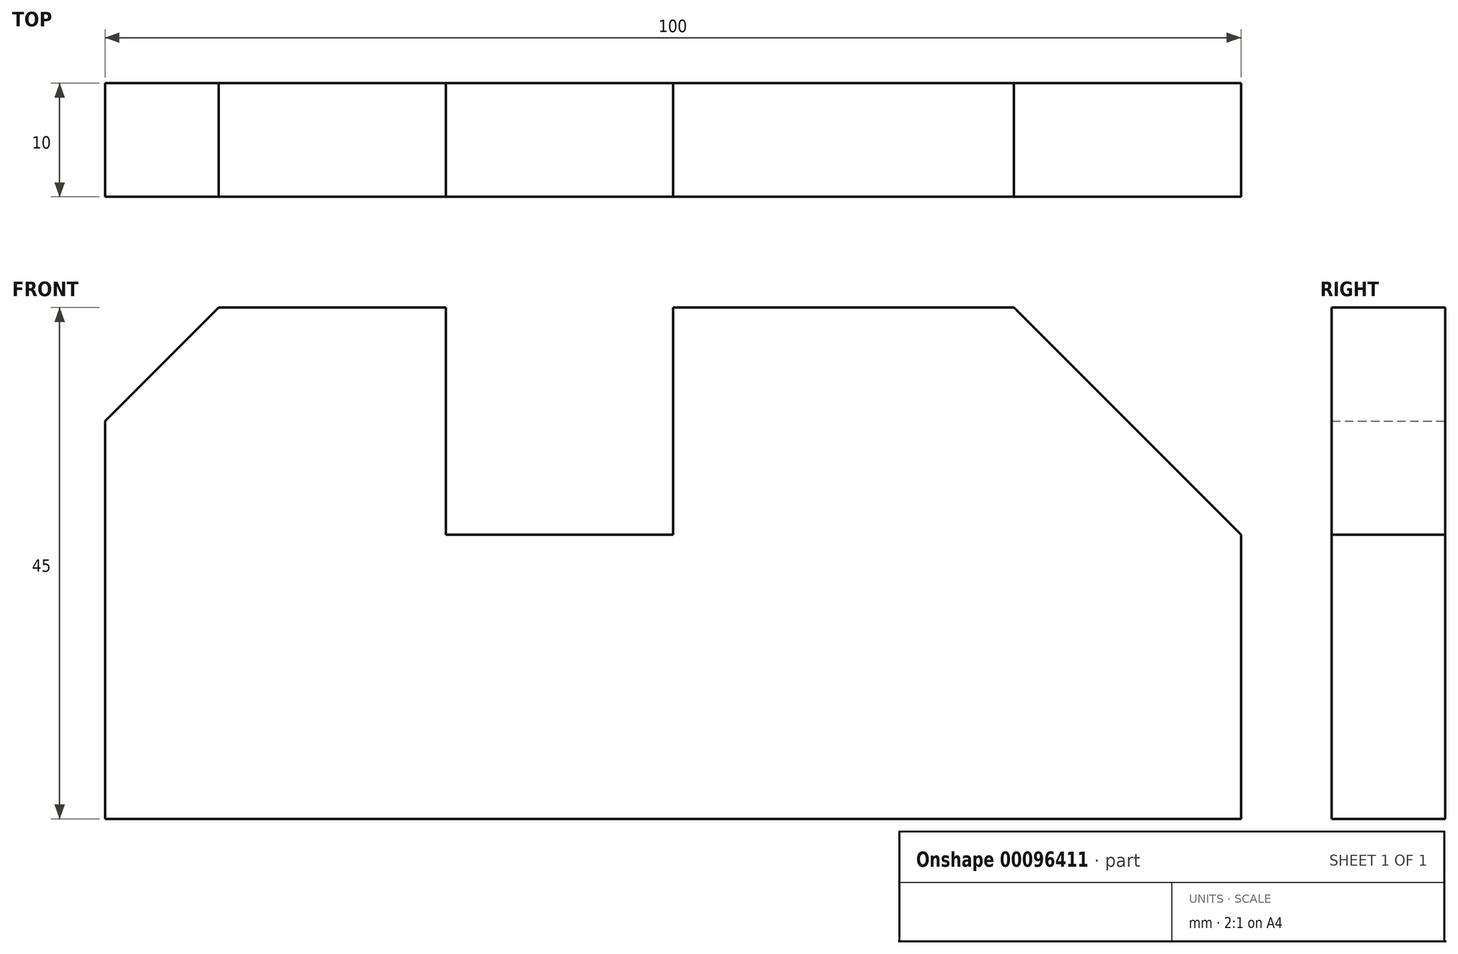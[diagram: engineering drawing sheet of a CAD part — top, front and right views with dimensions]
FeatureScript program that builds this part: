
annotation { "Feature Type Name" : "Feature", "Feature Type Description" : "" }
export const myFeature = defineFeature(function(context is Context, id is Id, definition is map)
    precondition{}
    {
        {
            var Q0;
            Q0=qCreatedBy(makeId("Front.planeOp"),FACE);
            var sketch = newSketch(context, id + "F0", { "sketchPlane" : qUnion([Q0])});
            skLineSegment(sketch, "E0", {"start": v(0, 0) * mm, "end": v(100, 0) * mm});
            skLineSegment(sketch, "E1", {"start": v(100, 0) * mm, "end": v(100, 25) * mm});
            skLineSegment(sketch, "E2", {"start": v(100, 25) * mm, "end": v(80, 45) * mm});
            skLineSegment(sketch, "E3", {"start": v(80, 45) * mm, "end": v(50, 45) * mm});
            skLineSegment(sketch, "E4", {"start": v(50, 45) * mm, "end": v(50, 25) * mm});
            skLineSegment(sketch, "E5", {"start": v(50, 25) * mm, "end": v(30, 25) * mm});
            skLineSegment(sketch, "E6", {"start": v(30, 25) * mm, "end": v(30, 45) * mm});
            skLineSegment(sketch, "E7", {"start": v(30, 45) * mm, "end": v(10, 45) * mm});
            skLineSegment(sketch, "E8", {"start": v(10, 45) * mm, "end": v(0, 35) * mm});
            skLineSegment(sketch, "E9", {"start": v(0, 35) * mm, "end": v(0, 0) * mm});
            skLineSegment(sketch, "E10", {"start": v(30, 45) * mm, "end": v(50, 45) * mm, "construction": true});
            skSolve(sketch);
        }
        {
            var Q0;
            Q0=makeQuery(id+"F0.imprint","IMPRINT",FACE,{"disambiguationData":[TD([[makeQuery(id+"F0.imprint","IMPRINT",EDGE,{"derivedFrom":sQuery(id+"F0.wireOp",EDGE,"E0")}),1.0]])]});
            var Q1;
            Q1=sQuery(id+"F0.wireOp",EDGE,"E4");
            var Q2;
            Q2=sQuery(id+"F0.wireOp",EDGE,"E5");
            var Q3;
            Q3=sQuery(id+"F0.wireOp",EDGE,"E9");
            var Q4;
            Q4=sQuery(id+"F0.wireOp",EDGE,"E6");
            var Q5;
            Q5=sQuery(id+"F0.wireOp",EDGE,"E7");
            var Q6;
            Q6=sQuery(id+"F0.wireOp",EDGE,"E3");
            var Q7;
            Q7=sQuery(id+"F0.wireOp",EDGE,"E1");
            var Q8;
            Q8=sQuery(id+"F0.wireOp",EDGE,"E0");
            var Q9;
            Q9=sQuery(id+"F0.wireOp",EDGE,"E2");
            var Q10;
            Q10=sQuery(id+"F0.wireOp",EDGE,"E8");
            extrude(context, id + "F1", {"entities" : qUnion([Q0]), "surfaceEntities" : qUnion([Q1, Q2, Q3, Q4, Q5, Q6, Q7, Q8, Q9, Q10]), "depth" : 10 * mm});
        }
    });
